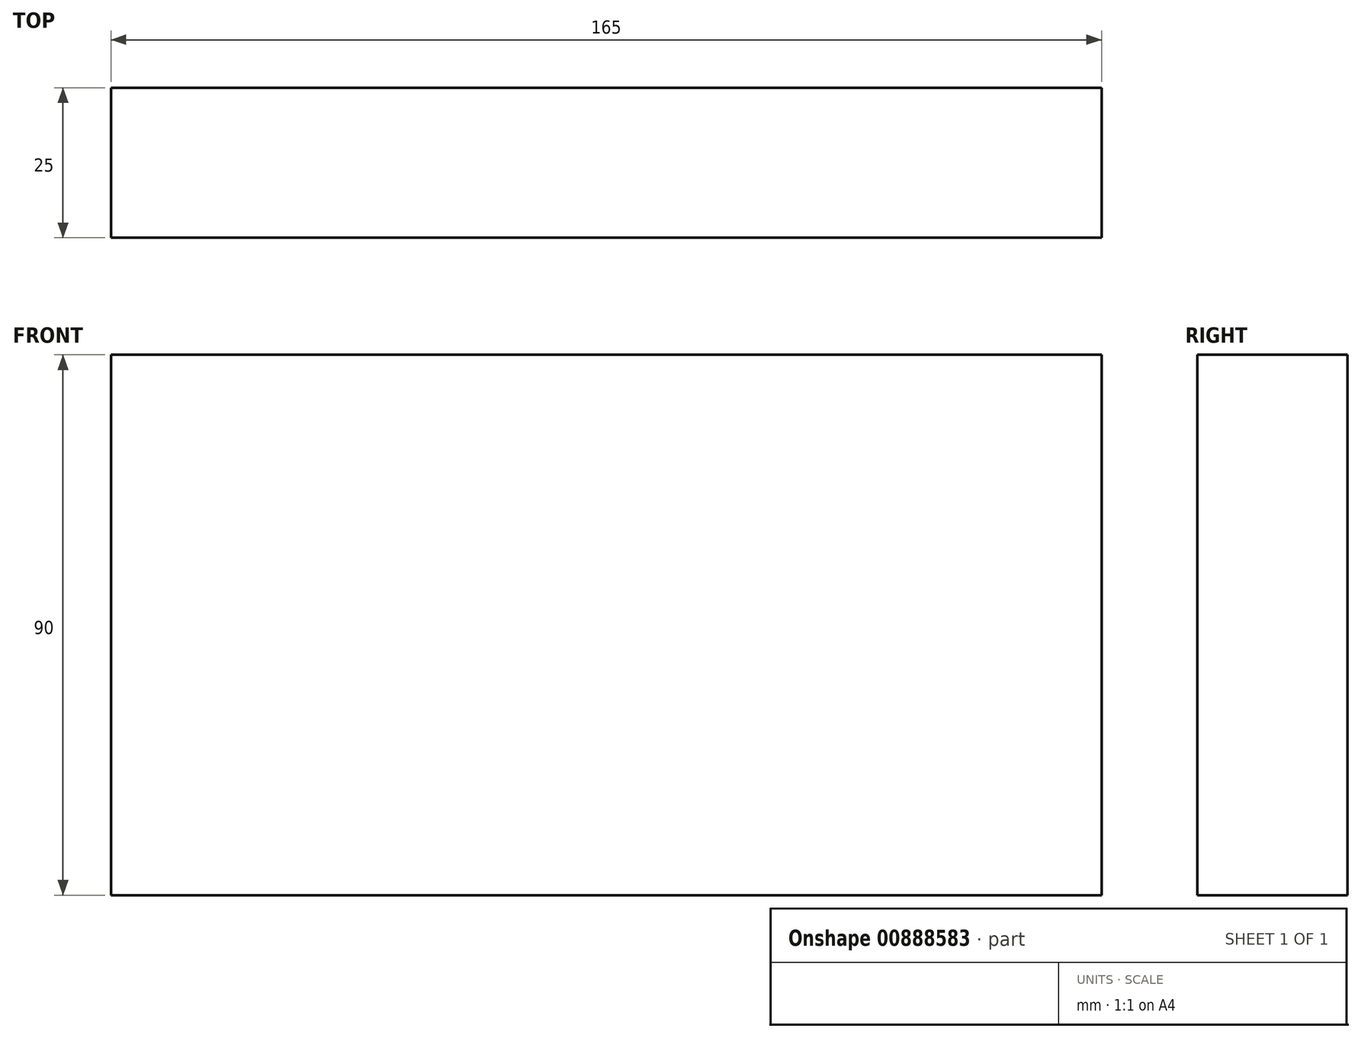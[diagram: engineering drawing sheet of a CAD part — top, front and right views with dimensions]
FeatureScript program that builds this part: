
annotation { "Feature Type Name" : "Feature", "Feature Type Description" : "" }
export const myFeature = defineFeature(function(context is Context, id is Id, definition is map)
    precondition{}
    {
        {
            var Q0;
            Q0=qCreatedBy(makeId("Front.planeOp"),FACE);
            var sketch = newSketch(context, id + "F0", { "sketchPlane" : qUnion([Q0])});
            skLineSegment(sketch, "E0", {"start": v(0, 0) * mm, "end": v(83, 0) * mm});
            skLineSegment(sketch, "E1", {"start": v(0, 0) * mm, "end": v(-82, 0) * mm});
            skLineSegment(sketch, "E2", {"start": v(0, 0) * mm, "end": v(0, 45) * mm});
            skLineSegment(sketch, "E3", {"start": v(-82, 0) * mm, "end": v(0, 45) * mm});
            skLineSegment(sketch, "E4", {"start": v(0, 45) * mm, "end": v(83, 0) * mm});
            skLineSegment(sketch, "E5", {"start": v(-82, 0) * mm, "end": v(-82, 90) * mm});
            skLineSegment(sketch, "E6", {"start": v(83, 0) * mm, "end": v(83, 90) * mm});
            skLineSegment(sketch, "E7", {"start": v(-82, 90) * mm, "end": v(0, 90) * mm});
            skLineSegment(sketch, "E8", {"start": v(0, 90) * mm, "end": v(83, 90) * mm});
            skLineSegment(sketch, "E9", {"start": v(-82, 90) * mm, "end": v(0, 45.54) * mm});
            skLineSegment(sketch, "E10", {"start": v(83, 90) * mm, "end": v(1.99, 45.54) * mm});
            skLineSegment(sketch, "E11", {"start": v(0, 90) * mm, "end": v(0, 45) * mm});
            skSolve(sketch);
        }
        {
            var Q0;
            Q0 = qSketchRegion(id + "F0", true);
            extrude(context, id + "F1", {"entities" : qUnion([Q0]), "depth" : 25 * mm, "offsetDistance" : 25 * mm});
        }
    });
